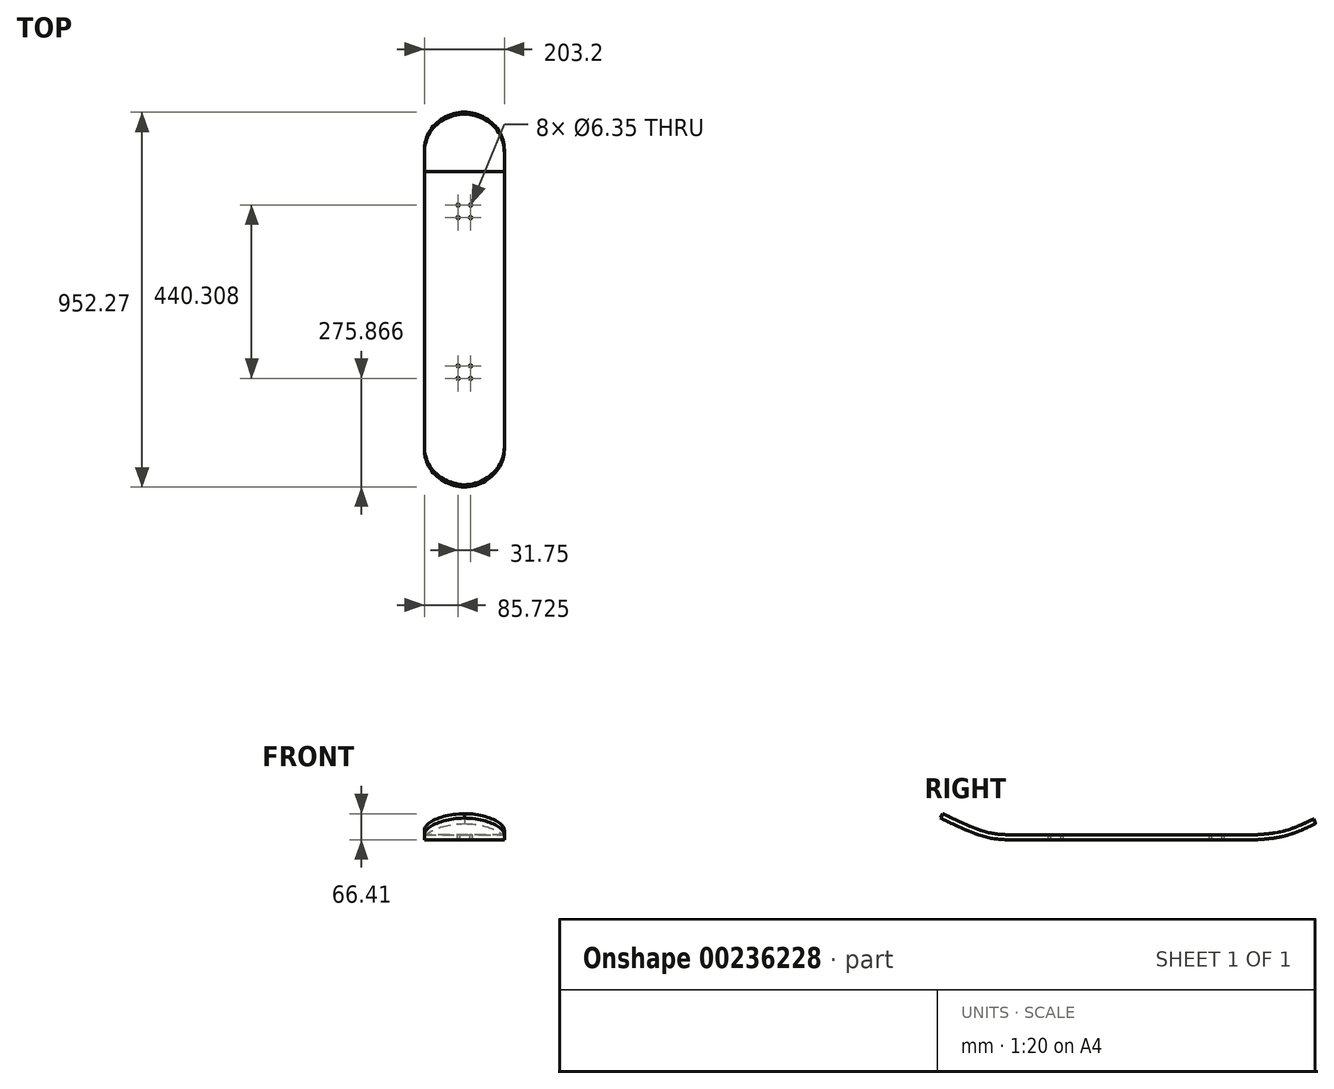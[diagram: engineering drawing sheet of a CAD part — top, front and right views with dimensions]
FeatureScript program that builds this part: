
annotation { "Feature Type Name" : "Feature", "Feature Type Description" : "" }
export const myFeature = defineFeature(function(context is Context, id is Id, definition is map)
    precondition{}
    {
        {
            var Q0;
            Q0=qCreatedBy(makeId("Top.planeOp"),FACE);
            var sketch = newSketch(context, id + "F0", { "sketchPlane" : qUnion([Q0])});
            skLineSegment(sketch, "E0.bottom", {"start": v(101.6, -304.8) * mm, "end": v(-101.6, -304.8) * mm});
            skLineSegment(sketch, "E0.top", {"start": v(101.6, 304.8) * mm, "end": v(-101.6, 304.8) * mm});
            skLineSegment(sketch, "E0.left", {"start": v(101.6, -304.8) * mm, "end": v(101.6, 304.8) * mm});
            skLineSegment(sketch, "E0.right", {"start": v(-101.6, -304.8) * mm, "end": v(-101.6, 304.8) * mm});
            skPoint(sketch, "E0.middle", {"position": v(0, 0) * mm});
            skPoint(sketch, "E1.middle", {"position": v(0, 204.28) * mm});
            skCircle(sketch, "E2", {"center": v(-15.88, 220.15) * mm, "radius": 3.18 * mm});
            skCircle(sketch, "E3", {"center": v(15.87, 220.15) * mm, "radius": 3.18 * mm});
            skCircle(sketch, "E4", {"center": v(15.87, 188.4) * mm, "radius": 3.18 * mm});
            skCircle(sketch, "E5", {"center": v(-15.88, 188.4) * mm, "radius": 3.18 * mm});
            skPoint(sketch, "E1.left.end.orphan", {"position": v(-25.4, 229.68) * mm});
            skPoint(sketch, "E1.bottom.start.orphan", {"position": v(-25.4, 178.88) * mm});
            skPoint(sketch, "E1.right.end.orphan", {"position": v(25.4, 229.68) * mm});
            skPoint(sketch, "E1.right.start.orphan", {"position": v(25.4, 178.88) * mm});
            skPoint(sketch, "E6.MirrorP", {"position": v(0, -204.28) * mm});
            skCircle(sketch, "E7.MirrorC", {"center": v(-15.88, -188.4) * mm, "radius": 3.18 * mm});
            skCircle(sketch, "E8.MirrorC", {"center": v(15.87, -188.4) * mm, "radius": 3.18 * mm});
            skCircle(sketch, "E9.MirrorC", {"center": v(15.87, -220.15) * mm, "radius": 3.18 * mm});
            skCircle(sketch, "E10.MirrorC", {"center": v(-15.88, -220.15) * mm, "radius": 3.18 * mm});
            skPoint(sketch, "E11.MirrorP", {"position": v(25.4, -229.68) * mm});
            skPoint(sketch, "E12.MirrorP", {"position": v(25.4, -178.88) * mm});
            skPoint(sketch, "E13.MirrorP", {"position": v(-25.4, -178.88) * mm});
            skPoint(sketch, "E14.MirrorP", {"position": v(-25.4, -229.68) * mm});
            skSolve(sketch);
        }
        {
            var Q0;
            Q0 = qSketchRegion(id + "F0", true);
            extrude(context, id + "F1", {"entities" : qUnion([Q0]), "endBound" : BoundingType.SYMMETRIC, "depth" : 12.7 * mm});
        }
        {
            var Q0;
            Q0=qCreatedBy(makeId("Right.planeOp"),FACE);
            var sketch = newSketch(context, id + "F2", { "sketchPlane" : qUnion([Q0])});
            skFitSpline(sketch, "E15", {"points": [v(304.83, 0) * mm, v(379.98, 10.33) * mm, v(453.97, 40.68) * mm], "startDerivative": vector(153.86, 11.33) * mm, "endDerivative": vector(144.47, 69.76) * mm});
            skSolve(sketch);
        }
        {
            var Q0;
            Q0=makeQuery(id+"F1.opExtrude","SWEPT_FACE",FACE,{"disambiguationData":[OSD([sQuery(id+"F0.wireOp",EDGE,"E0.top")])]});
            var Q1;
            Q1=sQuery(id+"F2.wireOp",EDGE,"4f9b5257-7dd3-4261-8318-3de27f794b43");
            var Q2;
            Q2=sQuery(id+"F2.wireOp",EDGE,"E15");
            sweep(context, id + "F3", {"operationType" : NewBodyOperationType.ADD, "profiles" : qUnion([Q0]), "path" : qUnion([Q1, Q2])});
        }
        {
            var Q0;
            Q0=makeQuery(id+"F3.opSweep","CAP_EDGE",EDGE,{"disambiguationData":[OSD([sQuery(id+"F0.wireOp",EDGE,"E0.top"),sQuery(id+"F0.wireOp",EDGE,"E0.right"),sQuery(id+"F2.wireOp",VERTEX,"E15.end")])],"isStart":false});
            var Q1;
            Q1=makeQuery(id+"F3.opSweep","CAP_EDGE",EDGE,{"disambiguationData":[OSD([sQuery(id+"F0.wireOp",EDGE,"E0.top"),sQuery(id+"F0.wireOp",EDGE,"E0.left"),sQuery(id+"F2.wireOp",VERTEX,"E15.end")])],"isStart":false});
            fillet(context, id + "F4", {"entities" : qUnion([Q0, Q1]), "radius" : 104.25 * mm, "tangentPropagation" : true, "allowEdgeOverflow" : false});
        }
        {
            var Q0;
            Q0=qCreatedBy(makeId("Right.planeOp"),FACE);
            var sketch = newSketch(context, id + "F5", { "sketchPlane" : qUnion([Q0])});
            skFitSpline(sketch, "E16", {"points": [v(-304.6, 0) * mm, v(-378.03, 6.38) * mm, v(-493.27, 54.38) * mm], "startDerivative": vector(-161.44, -0.57) * mm, "endDerivative": vector(-213.62, 104.74) * mm});
            skSolve(sketch);
        }
        {
            var Q0;
            Q0=makeQuery(id+"F1.opExtrude","SWEPT_FACE",FACE,{"disambiguationData":[OSD([sQuery(id+"F0.wireOp",EDGE,"E0.bottom")])]});
            var Q1;
            Q1=sQuery(id+"F5.wireOp",EDGE,"E16");
            sweep(context, id + "F6", {"operationType" : NewBodyOperationType.ADD, "profiles" : qUnion([Q0]), "path" : qUnion([Q1])});
        }
        {
            var Q0;
            Q0=makeQuery(id+"F6.opSweep","CAP_EDGE",EDGE,{"disambiguationData":[OSD([sQuery(id+"F0.wireOp",EDGE,"E0.bottom"),sQuery(id+"F0.wireOp",EDGE,"E0.left"),sQuery(id+"F5.wireOp",VERTEX,"E16.end")])],"isStart":false});
            var Q1;
            Q1=makeQuery(id+"F6.opSweep","CAP_EDGE",EDGE,{"disambiguationData":[OSD([sQuery(id+"F0.wireOp",EDGE,"E0.bottom"),sQuery(id+"F0.wireOp",EDGE,"E0.right"),sQuery(id+"F5.wireOp",VERTEX,"E16.end")])],"isStart":false});
            fillet(context, id + "F7", {"entities" : qUnion([Q0, Q1]), "radius" : 105.47 * mm, "tangentPropagation" : true, "allowEdgeOverflow" : false});
        }
    });
